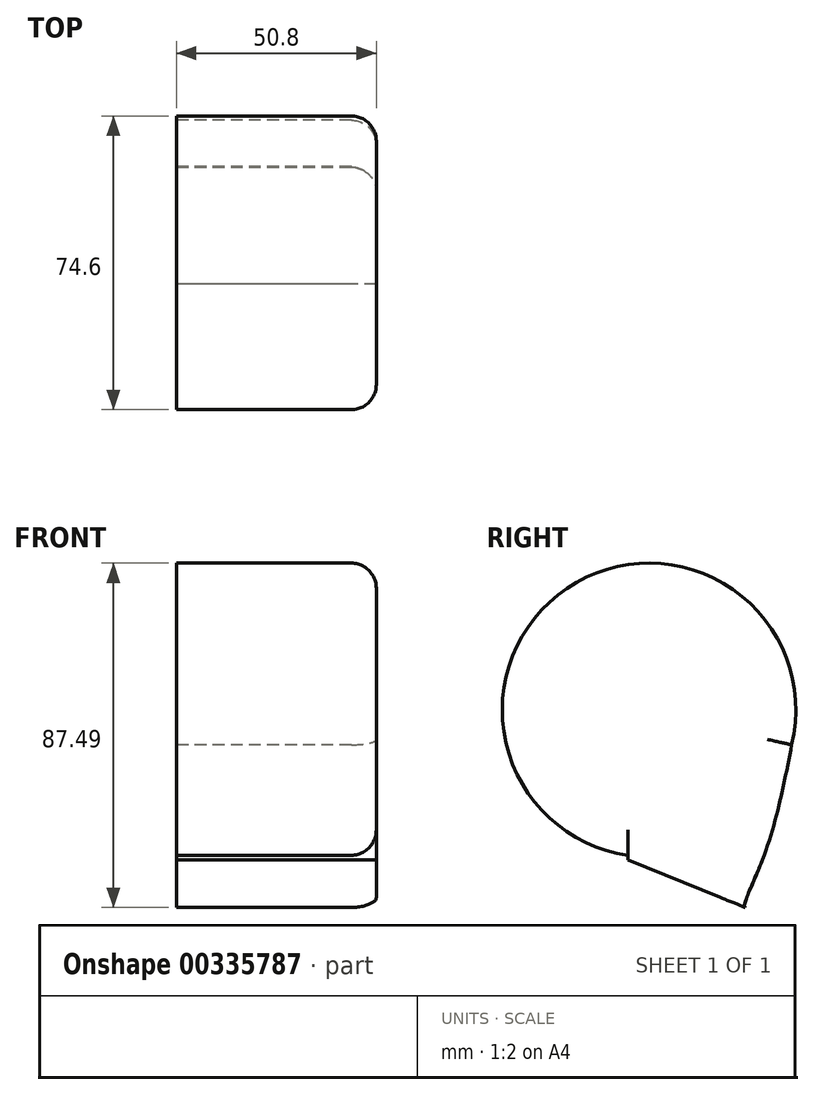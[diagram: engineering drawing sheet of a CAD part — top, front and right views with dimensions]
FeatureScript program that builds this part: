
annotation { "Feature Type Name" : "Feature", "Feature Type Description" : "" }
export const myFeature = defineFeature(function(context is Context, id is Id, definition is map)
    precondition{}
    {
        {
            var Q0;
            Q0=qCreatedBy(makeId("Right.planeOp"),FACE);
            var sketch = newSketch(context, id + "F0", { "sketchPlane" : qUnion([Q0])});
            skLineSegment(sketch, "E0.bottom", {"start": v(-38.1, 47.3) * mm, "end": v(38.1, 47.3) * mm});
            skLineSegment(sketch, "E0.top", {"start": v(-38.1, -28.9) * mm, "end": v(38.1, -28.9) * mm});
            skLineSegment(sketch, "E0.left", {"start": v(-38.1, 47.3) * mm, "end": v(-38.1, -28.9) * mm});
            skLineSegment(sketch, "E0.right", {"start": v(38.1, 47.3) * mm, "end": v(38.1, -28.9) * mm});
            skCircle(sketch, "E1", {"center": v(0, 9.2) * mm, "radius": 37.3 * mm});
            skPoint(sketch, "E1.centerSnap0", {"position": v(38.1, 9.2) * mm});
            skPoint(sketch, "E1.centerSnap1", {"position": v(0, 47.3) * mm});
            skFitSpline(sketch, "E2", {"points": [v(36.23, 0.34) * mm, v(28.8, -28.9) * mm, v(24.4, -41) * mm, v(38.1, -28.9) * mm], "startDerivative": vector(-14.25, -73.4) * mm, "endDerivative": vector(59.6, 59.88) * mm});
            skLineSegment(sketch, "E3", {"start": v(24.4, -41) * mm, "end": v(-5.33, -28.9) * mm});
            skPoint(sketch, "E3.endSnap0", {"position": v(0, -28.9) * mm});
            skLineSegment(sketch, "E4", {"start": v(-5.33, -28.9) * mm, "end": v(-5.33, -10.84) * mm});
            skSolve(sketch);
        }
        {
            var Q0;
            {var subQ0=sQuery(id+"F0.wireOp",EDGE,"E1");var subQ1=makeQuery(id+"F0.imprint","INTERSECT",VERTEX,{"derivedFrom":[subQ0,sQuery(id+"F0.wireOp",EDGE,"E2")]});Q0=makeQuery(id+"F0.imprint","IMPRINT",FACE,{"disambiguationData":[TD([[makeQuery(id+"F0.imprint","IMPRINT",EDGE,{"disambiguationData":[TD([[subQ1,1.0]])],"derivedFrom":subQ0}),1.0]])]});}
            var Q1;
            {var subQ0=sQuery(id+"F0.wireOp",EDGE,"E3");Q1=makeQuery(id+"F0.imprint","IMPRINT",FACE,{"disambiguationData":[TD([[makeQuery(id+"F0.imprint","IMPRINT",EDGE,{"derivedFrom":subQ0}),-1.0]])]});}
            var Q2;
            {var subQ3=sQuery(id+"F0.wireOp",EDGE,"E2");var subQ5=sQuery(id+"F0.wireOp",EDGE,"E1");var subQ7=makeQuery(id+"F0.imprint","INTERSECT",VERTEX,{"derivedFrom":[subQ5,subQ3]});Q2=makeQuery(id+"F0.imprint","IMPRINT",FACE,{"disambiguationData":[TD([[makeQuery(id+"F0.imprint","IMPRINT",EDGE,{"disambiguationData":[TD([[subQ7,1.0]])],"derivedFrom":subQ5}),-1.0]])]});}
            extrude(context, id + "F1", {"entities" : qUnion([Q0, Q1, Q2]), "depth" : 50.8 * mm});
        }
        {
            var Q0;
            Q0=makeQuery(id+"F1.opExtrude","CAP_EDGE",EDGE,{"disambiguationData":[OSD([sQuery(id+"F0.wireOp",EDGE,"E1")])],"isStart":false});
            fillet(context, id + "F2", {"entities" : qUnion([Q0]), "radius" : 6.35 * mm, "tangentPropagation" : true, "allowEdgeOverflow" : false});
        }
    });
